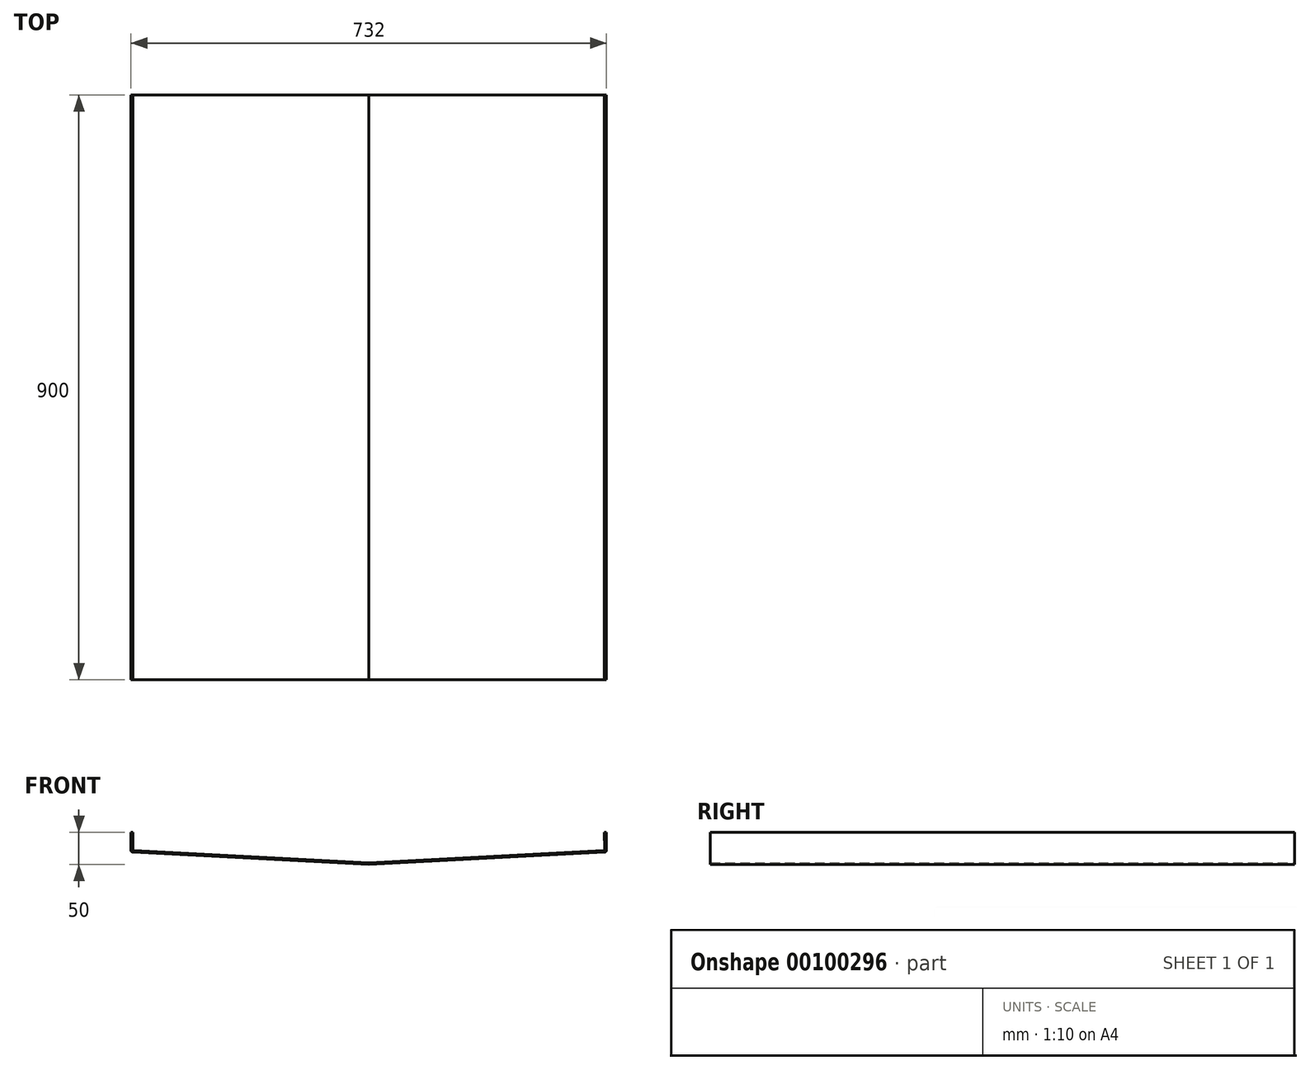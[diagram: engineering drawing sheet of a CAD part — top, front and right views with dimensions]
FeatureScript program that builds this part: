
annotation { "Feature Type Name" : "Feature", "Feature Type Description" : "" }
export const myFeature = defineFeature(function(context is Context, id is Id, definition is map)
    precondition{}
    {
        {
            var Q0;
            Q0=qCreatedBy(makeId("Front.planeOp"),FACE);
            var sketch = newSketch(context, id + "F0", { "sketchPlane" : qUnion([Q0])});
            skLineSegment(sketch, "E0", {"start": v(0, 0) * mm, "end": v(-363.16, 19.03) * mm});
            skLineSegment(sketch, "E1", {"start": v(0, 0) * mm, "end": v(0, 3) * mm, "construction": true});
            skLineSegment(sketch, "E2", {"start": v(0, 3) * mm, "end": v(-361.58, 21.95) * mm});
            skLineSegment(sketch, "E3", {"start": v(0, 3) * mm, "end": v(361.65, 21.95) * mm});
            skLineSegment(sketch, "E4", {"start": v(0, 0) * mm, "end": v(363.16, 19.03) * mm});
            skLineSegment(sketch, "E5", {"start": v(-366, -18.4) * mm, "end": v(-366, 67.98) * mm, "construction": true});
            skLineSegment(sketch, "E6", {"start": v(-363, -18.4) * mm, "end": v(-363, 67.94) * mm, "construction": true});
            skLineSegment(sketch, "E7", {"start": v(366, -18.4) * mm, "end": v(366, 70.67) * mm, "construction": true});
            skLineSegment(sketch, "E8", {"start": v(363, -18.4) * mm, "end": v(363, 69.98) * mm, "construction": true});
            skLineSegment(sketch, "E9", {"start": v(-363, 50) * mm, "end": v(-366, 50) * mm});
            skLineSegment(sketch, "E10", {"start": v(-366, 50) * mm, "end": v(-366, 22.03) * mm});
            skLineSegment(sketch, "E11", {"start": v(-363, 23.45) * mm, "end": v(-363, 50) * mm});
            skLineSegment(sketch, "E12", {"start": v(363.07, 23.45) * mm, "end": v(363, 50) * mm});
            skLineSegment(sketch, "E13", {"start": v(363, 50) * mm, "end": v(366, 50) * mm});
            skLineSegment(sketch, "E14", {"start": v(366, 50) * mm, "end": v(366, 22.03) * mm});
            skPoint(sketch, "E15.visualSharp", {"position": v(-366, 19.18) * mm});
            skArc(sketch, "E15.filletArc", {"start": v(-366, 22.03) * mm, "mid": v(-365.18, 19.96) * mm, "end": v(-363.16, 19.03) * mm});
            skPoint(sketch, "E16.visualSharp", {"position": v(366, 19.18) * mm});
            skArc(sketch, "E16.filletArc", {"start": v(363.16, 19.03) * mm, "mid": v(365.18, 19.96) * mm, "end": v(366, 22.03) * mm});
            skPoint(sketch, "E17.visualSharp", {"position": v(363.07, 22.03) * mm});
            skArc(sketch, "E17.filletArc", {"start": v(361.65, 21.95) * mm, "mid": v(362.66, 22.42) * mm, "end": v(363.07, 23.45) * mm});
            skPoint(sketch, "E18.visualSharp", {"position": v(-363, 22.02) * mm});
            skArc(sketch, "E18.filletArc", {"start": v(-363, 23.45) * mm, "mid": v(-362.59, 22.41) * mm, "end": v(-361.58, 21.95) * mm});
            skLineSegment(sketch, "E19", {"start": v(-366, 50) * mm, "end": v(366, 50) * mm, "construction": true});
            skSolve(sketch);
        }
        {
            var Q0;
            Q0=makeQuery(id+"F0.imprint","IMPRINT",FACE,{"disambiguationData":[TD([[makeQuery(id+"F0.imprint","IMPRINT",EDGE,{"derivedFrom":sQuery(id+"F0.wireOp",EDGE,"E0")}),-1.0]])]});
            extrude(context, id + "F1", {"entities" : qUnion([Q0]), "depth" : 900 * mm});
        }
    });
